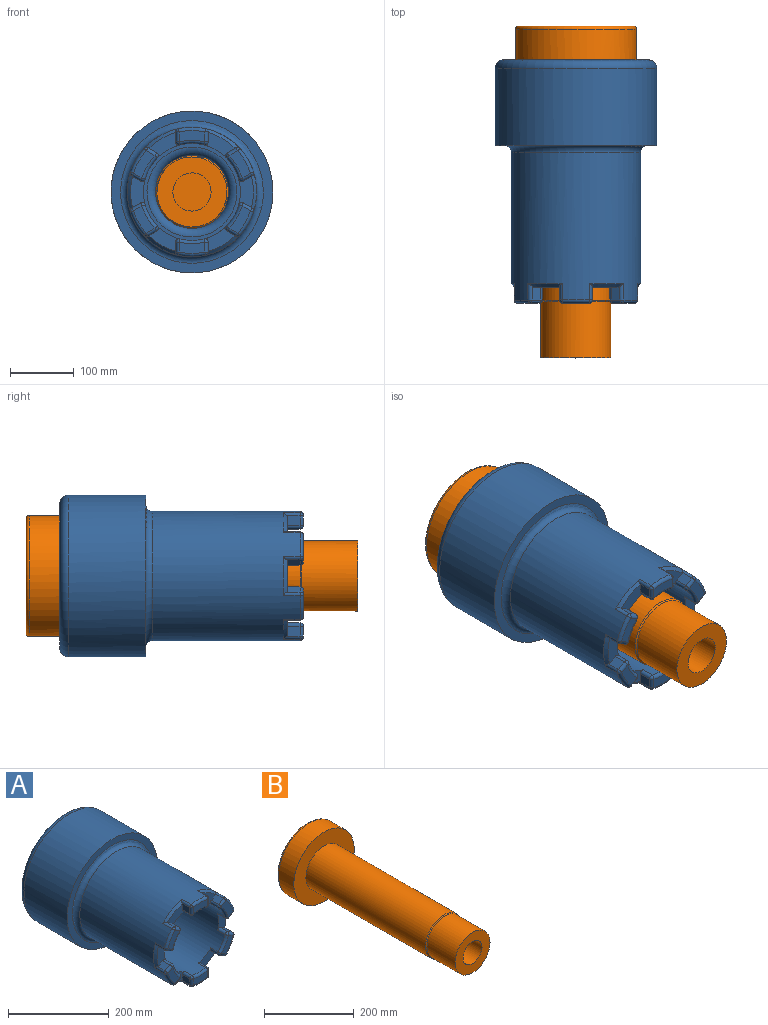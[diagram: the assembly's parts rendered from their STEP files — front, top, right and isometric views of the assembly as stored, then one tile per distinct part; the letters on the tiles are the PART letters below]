
ASSEMBLY  parts=2 mates=1
PART A: 113 faces, bbox 274.9x382.3x274.9 mm
  f0: plane 48.89x39.73mm, normal (0,-1,0), area 810.5mm2, adj f14,f17,f22,f93,f95,f110
  f1: plane 49.12x23.1mm, normal (0,-1,0), area 810.5mm2, adj f14,f78,f80,f92,f97,f109
  f2: plane 48.89x39.73mm, normal (0,-1,0), area 810.5mm2, adj f14,f63,f65,f77,f82,f108
  f3: plane 48.89x39.73mm, normal (0,-1,0), area 810.5mm2, adj f14,f48,f50,f62,f67,f107
  f4: plane 49.12x23.1mm, normal (0,-1,0), area 810.5mm2, adj f14,f33,f35,f47,f52,f111
  f5: plane 48.89x39.73mm, normal (0,-1,0), area 810.5mm2, adj f14,f18,f20,f32,f37,f112
  f6: plane 152.4x152.4mm, normal (0,-1,0), area 2564.6mm2, adj f11,f14
  f7: cylinder r=127mm len=254mm, axis (0,1,0), area 96656.9mm2, adj f8,f13
  f8: plane 254x254mm, normal (0,-1,0), area 11245.3mm2, adj f7,f16
  f9: plane 227.02x227.02mm, normal (0,1,0), area 24800.6mm2, adj f12,f13
  f10: cylinder r=57.15mm len=114.3mm, axis (0,1,0), area 38651.4mm2, adj f11,f12
  f11: torus R=70.64mm, axis (0,-1,0), area 8262.1mm2, adj f6,f10
  f12: torus R=70.64mm, axis (0,-1,0), area 8262.1mm2, adj f9,f10
  f13: torus R=113.51mm, axis (0,-1,0), area 16257mm2, adj f7,f9
  f14: cylinder r=76.2mm len=242.57mm, axis (0,1,0), area 111103.5mm2, adj f0,f1,f2,f3,f4,f5,f6,f20
  f15: cylinder r=101.6mm len=232.15mm, axis (0,1,0), area 138549.1mm2, adj f16,f25,f29,f31,f40,f44,f46,f55
  f16: torus R=112.02mm, axis (0,-1,0), area 10843mm2, adj f8,f15
  f17: plane 21.52x15.66mm, normal (1,0,0), area 318.9mm2, adj f0,f22,f28,f31,f110
  f18: plane 21.52x15.66mm, normal (-1,0,0), area 318.9mm2, adj f5,f20,f24,f25,f112
  f19: plane 40.64x17.82mm, normal (0,-1,0), area 624.9mm2, adj f23,f24,f28,f29
  f20: cylinder r=5.08mm len=20.32mm, axis (0,1,0), area 188.2mm2, adj f5,f14,f18,f21
  f21: sphere r=5.08mm, area 47.1mm2, adj f20,f23,f24
  f22: cylinder r=5.08mm len=20.32mm, axis (0,1,0), area 188.2mm2, adj f0,f14,f17,f26
  f23: torus R=81.28mm, axis (0,-1,0), area 314.7mm2, adj f14,f19,f21,f26
  f24: cylinder r=5.08mm len=15.66mm, axis (0,0,1), area 124.9mm2, adj f18,f19,f21,f27
  f25: cylinder r=5.08mm len=25.4mm, axis (0,1,0), area 165.9mm2, adj f15,f18,f27,f112
  f26: sphere r=5.08mm, area 47.1mm2, adj f22,f23,f28
  f27: sphere r=5.08mm, area 35.1mm2, adj f24,f25,f29
  f28: cylinder r=5.08mm len=15.66mm, axis (0,0,-1), area 124.9mm2, adj f17,f19,f26,f30
  f29: torus R=96.52mm, axis (0,-1,0), area 337.7mm2, adj f15,f19,f27,f30
  f30: sphere r=5.08mm, area 35.1mm2, adj f28,f29,f31
  f31: cylinder r=5.08mm len=25.4mm, axis (0,1,0), area 165.9mm2, adj f15,f17,f30,f110
  f32: plane 21.52x13.56mm, normal (0.5,0,0.87), area 318.9mm2, adj f5,f37,f43,f46,f112
  f33: plane 21.52x13.56mm, normal (-0.5,0,-0.87), area 318.9mm2, adj f4,f35,f39,f40,f111
  f34: plane 43.02x33.88mm, normal (0,-1,0), area 624.9mm2, adj f38,f39,f43,f44
  f35: cylinder r=5.08mm len=20.32mm, axis (0,1,0), area 188.2mm2, adj f4,f14,f33,f36
  f36: sphere r=5.08mm, area 47.1mm2, adj f35,f38,f39
  f37: cylinder r=5.08mm len=20.32mm, axis (0,1,0), area 188.2mm2, adj f5,f14,f32,f41
  f38: torus R=81.28mm, axis (0,-1,0), area 314.7mm2, adj f14,f34,f36,f41
  f39: cylinder r=5.08mm len=16.1mm, axis (-0.87,0,0.5), area 124.9mm2, adj f33,f34,f36,f42
  f40: cylinder r=5.08mm len=25.4mm, axis (0,1,0), area 165.9mm2, adj f15,f33,f42,f111
  f41: sphere r=5.08mm, area 47.1mm2, adj f37,f38,f43
  f42: sphere r=5.08mm, area 35.1mm2, adj f39,f40,f44
  f43: cylinder r=5.08mm len=16.1mm, axis (0.87,0,-0.5), area 124.9mm2, adj f32,f34,f41,f45
  f44: torus R=96.52mm, axis (0,-1,0), area 337.7mm2, adj f15,f34,f42,f45
  f45: sphere r=5.08mm, area 35.1mm2, adj f43,f44,f46
  f46: cylinder r=5.08mm len=25.4mm, axis (0,1,0), area 165.9mm2, adj f15,f32,f45,f112
  f47: plane 21.52x13.56mm, normal (-0.5,0,0.87), area 318.9mm2, adj f4,f52,f58,f61,f111
  f48: plane 21.52x13.56mm, normal (0.5,0,-0.87), area 318.9mm2, adj f3,f50,f54,f55,f107
  f49: plane 43.02x33.88mm, normal (0,-1,0), area 624.9mm2, adj f53,f54,f58,f59
  f50: cylinder r=5.08mm len=20.32mm, axis (0,1,0), area 188.2mm2, adj f3,f14,f48,f51
  f51: sphere r=5.08mm, area 47.1mm2, adj f50,f53,f54
  f52: cylinder r=5.08mm len=20.32mm, axis (0,1,0), area 188.2mm2, adj f4,f14,f47,f56
  f53: torus R=81.28mm, axis (0,-1,0), area 314.7mm2, adj f14,f49,f51,f56
  f54: cylinder r=5.08mm len=16.1mm, axis (-0.87,0,-0.5), area 124.9mm2, adj f48,f49,f51,f57
  f55: cylinder r=5.08mm len=25.4mm, axis (0,1,0), area 165.9mm2, adj f15,f48,f57,f107
  f56: sphere r=5.08mm, area 47.1mm2, adj f52,f53,f58
  f57: sphere r=5.08mm, area 35.1mm2, adj f54,f55,f59
  f58: cylinder r=5.08mm len=16.1mm, axis (0.87,0,0.5), area 124.9mm2, adj f47,f49,f56,f60
  f59: torus R=96.52mm, axis (0,-1,0), area 337.7mm2, adj f15,f49,f57,f60
  f60: sphere r=5.08mm, area 35.1mm2, adj f58,f59,f61
  f61: cylinder r=5.08mm len=25.4mm, axis (0,1,0), area 165.9mm2, adj f15,f47,f60,f111
  f62: plane 21.52x15.66mm, normal (-1,0,0), area 318.9mm2, adj f3,f67,f73,f76,f107
  f63: plane 21.52x15.66mm, normal (1,0,0), area 318.9mm2, adj f2,f65,f69,f70,f108
  f64: plane 40.64x17.82mm, normal (0,-1,0), area 624.9mm2, adj f68,f69,f73,f74
  f65: cylinder r=5.08mm len=20.32mm, axis (0,1,0), area 188.2mm2, adj f2,f14,f63,f66
  f66: sphere r=5.08mm, area 47.1mm2, adj f65,f68,f69
  f67: cylinder r=5.08mm len=20.32mm, axis (0,1,0), area 188.2mm2, adj f3,f14,f62,f71
  f68: torus R=81.28mm, axis (0,-1,0), area 314.7mm2, adj f14,f64,f66,f71
  f69: cylinder r=5.08mm len=15.66mm, axis (0,0,-1), area 124.9mm2, adj f63,f64,f66,f72
  f70: cylinder r=5.08mm len=25.4mm, axis (0,1,0), area 165.9mm2, adj f15,f63,f72,f108
  f71: sphere r=5.08mm, area 47.1mm2, adj f67,f68,f73
  f72: sphere r=5.08mm, area 35.1mm2, adj f69,f70,f74
  f73: cylinder r=5.08mm len=15.66mm, axis (0,0,1), area 124.9mm2, adj f62,f64,f71,f75
  f74: torus R=96.52mm, axis (0,-1,0), area 337.7mm2, adj f15,f64,f72,f75
  f75: sphere r=5.08mm, area 35.1mm2, adj f73,f74,f76
  f76: cylinder r=5.08mm len=25.4mm, axis (0,1,0), area 165.9mm2, adj f15,f62,f75,f107
  f77: plane 21.52x13.56mm, normal (-0.5,0,-0.87), area 318.9mm2, adj f2,f82,f88,f91,f108
  f78: plane 21.52x13.56mm, normal (0.5,0,0.87), area 318.9mm2, adj f1,f80,f84,f85,f109
  f79: plane 43.02x33.88mm, normal (0,-1,0), area 624.9mm2, adj f83,f84,f88,f89
  f80: cylinder r=5.08mm len=20.32mm, axis (0,1,0), area 188.2mm2, adj f1,f14,f78,f81
  f81: sphere r=5.08mm, area 47.1mm2, adj f80,f83,f84
  f82: cylinder r=5.08mm len=20.32mm, axis (0,1,0), area 188.2mm2, adj f2,f14,f77,f86
  f83: torus R=81.28mm, axis (0,-1,0), area 314.7mm2, adj f14,f79,f81,f86
  f84: cylinder r=5.08mm len=16.1mm, axis (0.87,0,-0.5), area 124.9mm2, adj f78,f79,f81,f87
  f85: cylinder r=5.08mm len=25.4mm, axis (0,1,0), area 165.9mm2, adj f15,f78,f87,f109
  f86: sphere r=5.08mm, area 47.1mm2, adj f82,f83,f88
  f87: sphere r=5.08mm, area 35.1mm2, adj f84,f85,f89
  f88: cylinder r=5.08mm len=16.1mm, axis (-0.87,0,0.5), area 124.9mm2, adj f77,f79,f86,f90
  f89: torus R=96.52mm, axis (0,-1,0), area 337.7mm2, adj f15,f79,f87,f90
  f90: sphere r=5.08mm, area 35.1mm2, adj f88,f89,f91
  f91: cylinder r=5.08mm len=25.4mm, axis (0,1,0), area 165.9mm2, adj f15,f77,f90,f108
  f92: plane 21.52x13.56mm, normal (0.5,0,-0.87), area 318.9mm2, adj f1,f97,f103,f106,f109
  f93: plane 21.52x13.56mm, normal (-0.5,0,0.87), area 318.9mm2, adj f0,f95,f99,f100,f110
  f94: plane 43.02x33.88mm, normal (0,-1,0), area 624.9mm2, adj f98,f99,f103,f104
  f95: cylinder r=5.08mm len=20.32mm, axis (0,1,0), area 188.2mm2, adj f0,f14,f93,f96
  f96: sphere r=5.08mm, area 47.1mm2, adj f95,f98,f99
  f97: cylinder r=5.08mm len=20.32mm, axis (0,1,0), area 188.2mm2, adj f1,f14,f92,f101
  f98: torus R=81.28mm, axis (0,-1,0), area 314.7mm2, adj f14,f94,f96,f101
  f99: cylinder r=5.08mm len=16.1mm, axis (0.87,0,0.5), area 124.9mm2, adj f93,f94,f96,f102
  f100: cylinder r=5.08mm len=25.4mm, axis (0,1,0), area 165.9mm2, adj f15,f93,f102,f110
  f101: sphere r=5.08mm, area 47.1mm2, adj f97,f98,f103
  f102: sphere r=5.08mm, area 35.1mm2, adj f99,f100,f104
  f103: cylinder r=5.08mm len=16.1mm, axis (-0.87,0,-0.5), area 124.9mm2, adj f92,f94,f101,f105
  f104: torus R=96.52mm, axis (0,-1,0), area 337.7mm2, adj f15,f94,f102,f105
  f105: sphere r=5.08mm, area 35.1mm2, adj f103,f104,f106
  f106: cylinder r=5.08mm len=25.4mm, axis (0,1,0), area 165.9mm2, adj f15,f92,f105,f109
  f107: cone r=96.52mm half-angle=45deg, axis (0,1,0), area 385.2mm2, adj f3,f15,f48,f55,f62,f76
  f108: cone r=96.52mm half-angle=45deg, axis (0,1,0), area 385.2mm2, adj f2,f15,f63,f70,f77,f91
  f109: cone r=96.52mm half-angle=45deg, axis (0,1,0), area 385.2mm2, adj f1,f15,f78,f85,f92,f106
  f110: cone r=96.52mm half-angle=45deg, axis (0,1,0), area 385.2mm2, adj f0,f15,f17,f31,f93,f100
  f111: cone r=96.52mm half-angle=45deg, axis (0,1,0), area 385.2mm2, adj f4,f15,f33,f40,f47,f61
  f112: cone r=96.52mm half-angle=45deg, axis (0,1,0), area 385.2mm2, adj f5,f15,f18,f25,f32,f46
PART B: 10 faces, bbox 205.7x521x205.7 mm
  f0: cylinder r=57.15mm len=377.27mm, axis (0,1,0), area 135471.6mm2, adj f3,f9
  f1: cylinder r=95mm len=190.01mm, axis (0,-1,0), area 28652.5mm2, adj f3,f4
  f2: plane 180.01x180.01mm, normal (0,1,0), area 25449.2mm2, adj f4
  f3: plane 190.01x190.01mm, normal (0,-1,0), area 18094.4mm2, adj f0,f1
  f4: torus R=90mm, axis (0,-1,0), area 4598.6mm2, adj f1,f2
  f5: cylinder r=30mm len=85.7mm, axis (0,1,0), area 16154.1mm2, adj f7,f8
  f6: cylinder r=55mm len=110mm, axis (0,1,0), area 30600.7mm2, adj f7,f9
  f7: plane 110x110mm, normal (0,-1,0), area 6675.9mm2, adj f5,f6
  f8: plane 60x60mm, normal (0,-1,0), area 2827.4mm2, adj f5
  f9: cone r=52.15mm half-angle=45deg, axis (0,1,0), area 1071.3mm2, adj f0,f6
PLACE A t=(-0.08,-61.1,70.99)mm fixed
PLACE B rot(axis=(0,1,0),41.8deg) t=(-0.08,-61.16,70.99)mm
MATE cylindrical B.f0 <-> A.f7  axis (0,1,0) through (-0.08,-249.79,70.99)mm
